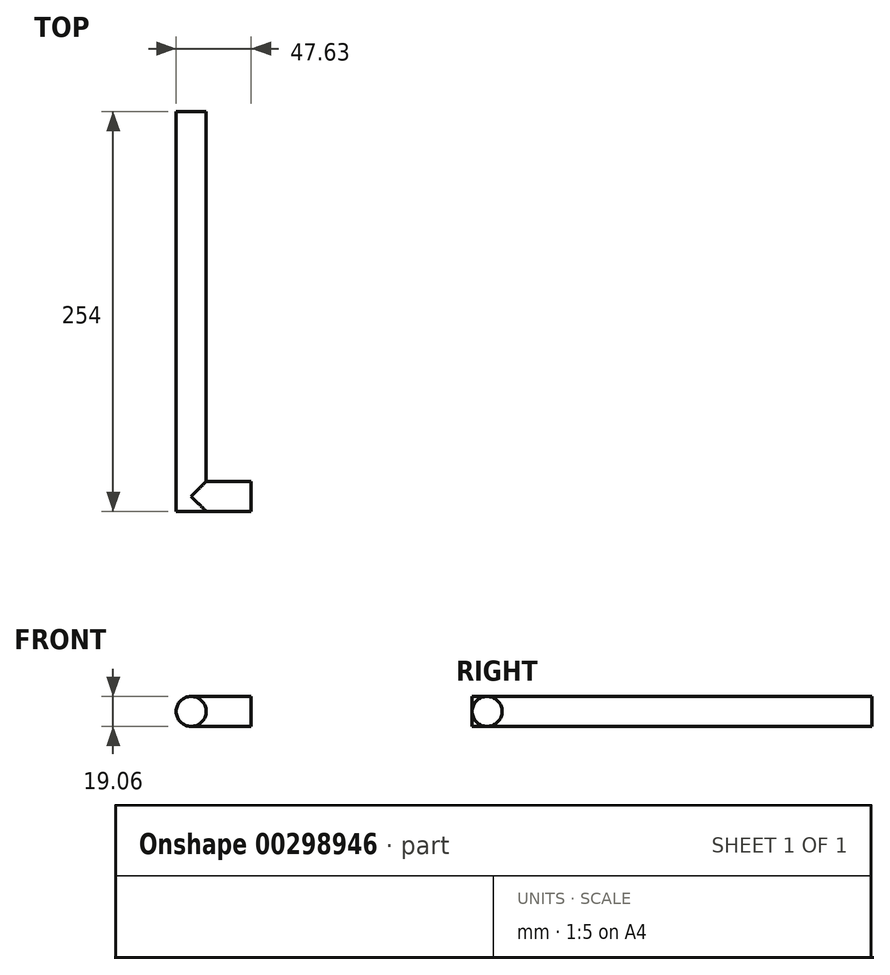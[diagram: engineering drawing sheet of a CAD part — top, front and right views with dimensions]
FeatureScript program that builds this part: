
annotation { "Feature Type Name" : "Feature", "Feature Type Description" : "" }
export const myFeature = defineFeature(function(context is Context, id is Id, definition is map)
    precondition{}
    {
        {
            var Q0;
            Q0=qCreatedBy(makeId("Front.planeOp"),FACE);
            var sketch = newSketch(context, id + "F0", { "sketchPlane" : qUnion([Q0])});
            skCircle(sketch, "E0", {"center": v(0, 0) * mm, "radius": 9.53 * mm});
            skSolve(sketch);
        }
        {
            var Q0;
            Q0=makeQuery(id+"F0.imprint","IMPRINT",FACE,{"disambiguationData":[TD([[makeQuery(id+"F0.imprint","IMPRINT",EDGE,{"derivedFrom":sQuery(id+"F0.wireOp",EDGE,"E0")}),1.0]])]});
            extrude(context, id + "F1", {"entities" : qUnion([Q0]), "oppositeDirection" : true, "depth" : 254 * mm});
        }
        {
            var Q0;
            Q0=qCreatedBy(makeId("Right.planeOp"),FACE);
            var sketch = newSketch(context, id + "F2", { "sketchPlane" : qUnion([Q0])});
            skCircle(sketch, "E1", {"center": v(9.53, 0) * mm, "radius": 9.53 * mm});
            skSolve(sketch);
        }
        {
            var Q0;
            Q0 = qSketchRegion(id + "F2", true);
            extrude(context, id + "F3", {"entities" : qUnion([Q0]), "operationType" : NewBodyOperationType.ADD, "depth" : 38.1 * mm});
        }
    });
